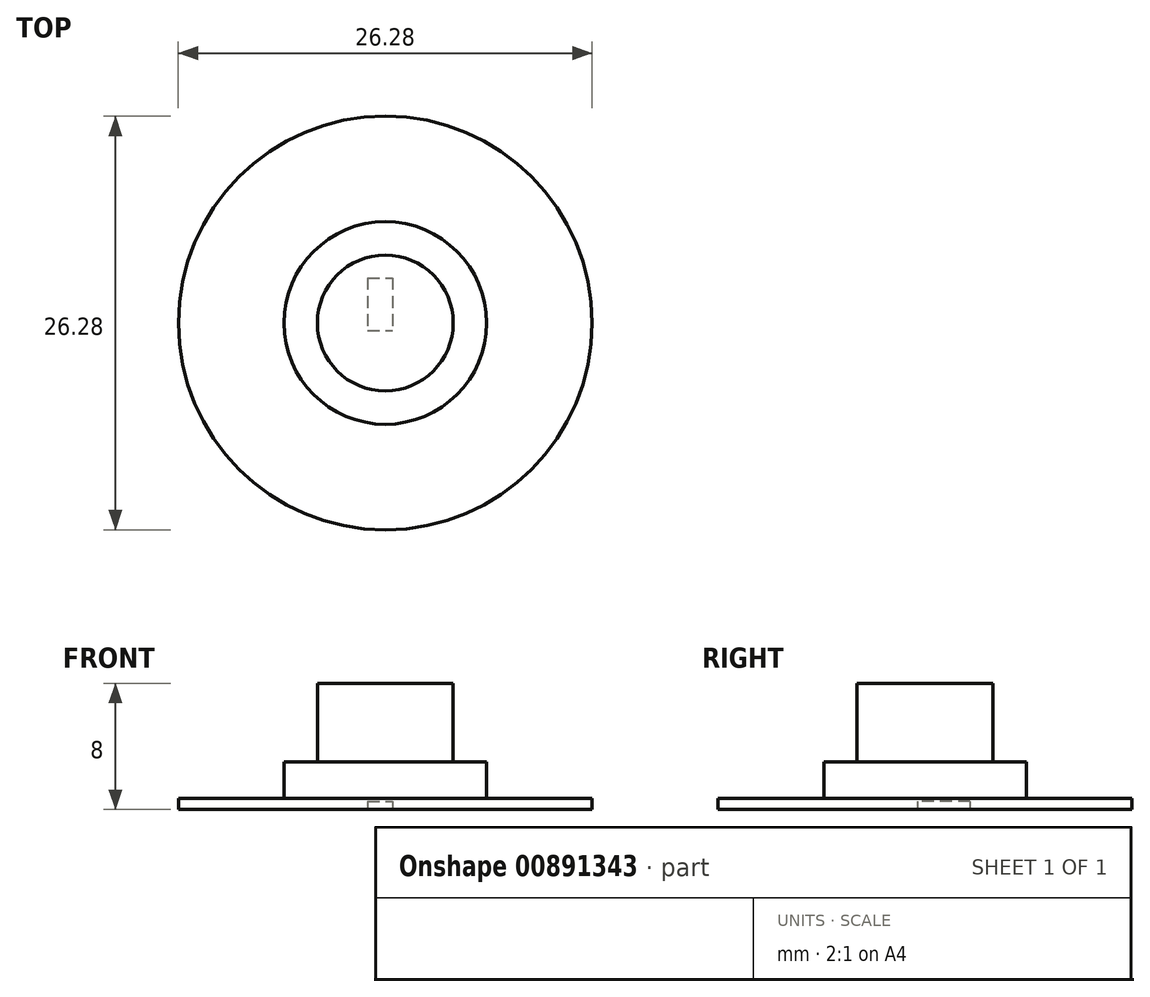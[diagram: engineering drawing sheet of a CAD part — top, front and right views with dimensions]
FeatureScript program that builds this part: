
annotation { "Feature Type Name" : "Feature", "Feature Type Description" : "" }
export const myFeature = defineFeature(function(context is Context, id is Id, definition is map)
    precondition{}
    {
        {
            var Q0;
            Q0=qCreatedBy(makeId("Top.planeOp"),FACE);
            var sketch = newSketch(context, id + "F0", { "sketchPlane" : qUnion([Q0])});
            skCircle(sketch, "E0", {"center": v(0, 0) * mm, "radius": 5 * mm});
            skCircle(sketch, "E1", {"center": v(0, 0) * mm, "radius": 4.33 * mm});
            skCircle(sketch, "E2", {"center": v(-35.7, -21.68) * mm, "radius": 4.32 * mm});
            skCircle(sketch, "E3", {"center": v(-35.7, -21.68) * mm, "radius": 6.43 * mm});
            skCircle(sketch, "E4", {"center": v(-35.7, -21.68) * mm, "radius": 13.14 * mm});
            skSolve(sketch);
        }
        {
            var Q0;
            Q0=makeQuery(id+"F0.imprint","IMPRINT",FACE,{"disambiguationData":[TD([[makeQuery(id+"F0.imprint","IMPRINT",EDGE,{"derivedFrom":sQuery(id+"F0.wireOp",EDGE,"E1")}),1.0]])]});
            extrude(context, id + "F1", {"entities" : qUnion([Q0]), "oppositeDirection" : true, "depth" : 3 * mm, "offsetDistance" : 25 * mm});
        }
        {
            var Q0;
            Q0 = qSketchRegion(id + "F0", true);
            var Q1;
            Q1=makeQuery(id+"F1.opExtrude","CAP_FACE",FACE,{"disambiguationData":[OSD([sQuery(id+"F0.wireOp",EDGE,"E1")])],"isStart":true});
            extrude(context, id + "F2", {"entities" : qUnion([Q0, Q1]), "operationType" : NewBodyOperationType.ADD, "depth" : 0.7 * mm, "offsetDistance" : 25 * mm});
        }
        {
            var Q0;
            Q0=makeQuery(id+"F0.imprint","IMPRINT",FACE,{"disambiguationData":[TD([[makeQuery(id+"F0.imprint","IMPRINT",EDGE,{"derivedFrom":sQuery(id+"F0.wireOp",EDGE,"E2")}),1.0]])]});
            extrude(context, id + "F3", {"entities" : qUnion([Q0]), "depth" : 8 * mm, "offsetDistance" : 25 * mm});
        }
        {
            var Q0;
            Q0=makeQuery(id+"F0.imprint","IMPRINT",FACE,{"disambiguationData":[TD([[makeQuery(id+"F0.imprint","IMPRINT",EDGE,{"derivedFrom":sQuery(id+"F0.wireOp",EDGE,"E2")}),-1.0]])]});
            extrude(context, id + "F4", {"entities" : qUnion([Q0]), "depth" : 3 * mm, "offsetDistance" : 25 * mm});
        }
        {
            var Q0;
            Q0=makeQuery(id+"F1.opExtrude","SWEPT_BODY",BODY,{"disambiguationData":[OSD([sQuery(id+"F0.wireOp",EDGE,"E1")])]});
            deleteBodies(context, id + "F5", {"entities" : qUnion([Q0])});
        }
        {
            var Q0;
            Q0=makeQuery(id+"F2.opExtrude","SWEPT_BODY",BODY,{"disambiguationData":[OSD([sQuery(id+"F0.wireOp",EDGE,"E3"),sQuery(id+"F0.wireOp",EDGE,"E4")])]});
            var Q1;
            Q1=makeQuery(id+"F3.opExtrude","SWEPT_BODY",BODY,{"disambiguationData":[OSD([sQuery(id+"F0.wireOp",EDGE,"E2")])]});
            var Q2;
            Q2=makeQuery(id+"F4.opExtrude","SWEPT_BODY",BODY,{"disambiguationData":[OSD([sQuery(id+"F0.wireOp",EDGE,"E2"),sQuery(id+"F0.wireOp",EDGE,"E3")])]});
            booleanBodies(context, id + "F6", {"operationType" : BooleanOperationType.UNION, "tools" : qUnion([Q0, Q1, Q2])});
        }
        {
            var Q0;
            {var subQ0=sQuery(id+"F0.wireOp",EDGE,"E3");var subQ1=sQuery(id+"F0.wireOp",EDGE,"E2");Q0=makeQuery(id+"F6.opBoolean","MERGE",FACE,{"derivedFrom":[makeQuery(id+"F2.opExtrude","CAP_FACE",FACE,{"disambiguationData":[OSD([subQ0,sQuery(id+"F0.wireOp",EDGE,"E4")])],"isStart":true}),makeQuery(id+"F3.opExtrude","CAP_FACE",FACE,{"disambiguationData":[OSD([subQ1])],"isStart":true}),makeQuery(id+"F4.opExtrude","CAP_FACE",FACE,{"disambiguationData":[OSD([subQ1,subQ0])],"isStart":true})]});}
            var sketch = newSketch(context, id + "F7", { "sketchPlane" : qUnion([Q0])});
            skLineSegment(sketch, "E5.bottom", {"start": v(-36.83, 18.82) * mm, "end": v(-35.25, 18.82) * mm});
            skLineSegment(sketch, "E5.top", {"start": v(-36.83, 22.16) * mm, "end": v(-35.25, 22.16) * mm});
            skLineSegment(sketch, "E5.left", {"start": v(-36.83, 18.82) * mm, "end": v(-36.83, 22.16) * mm});
            skLineSegment(sketch, "E5.right", {"start": v(-35.25, 18.82) * mm, "end": v(-35.25, 22.16) * mm});
            skSolve(sketch);
        }
        {
            var Q0;
            Q0 = qSketchRegion(id + "F7", true);
            extrude(context, id + "F8", {"entities" : qUnion([Q0]), "operationType" : NewBodyOperationType.REMOVE, "oppositeDirection" : true, "depth" : .5 * mm, "offsetDistance" : 25 * mm});
        }
    });
